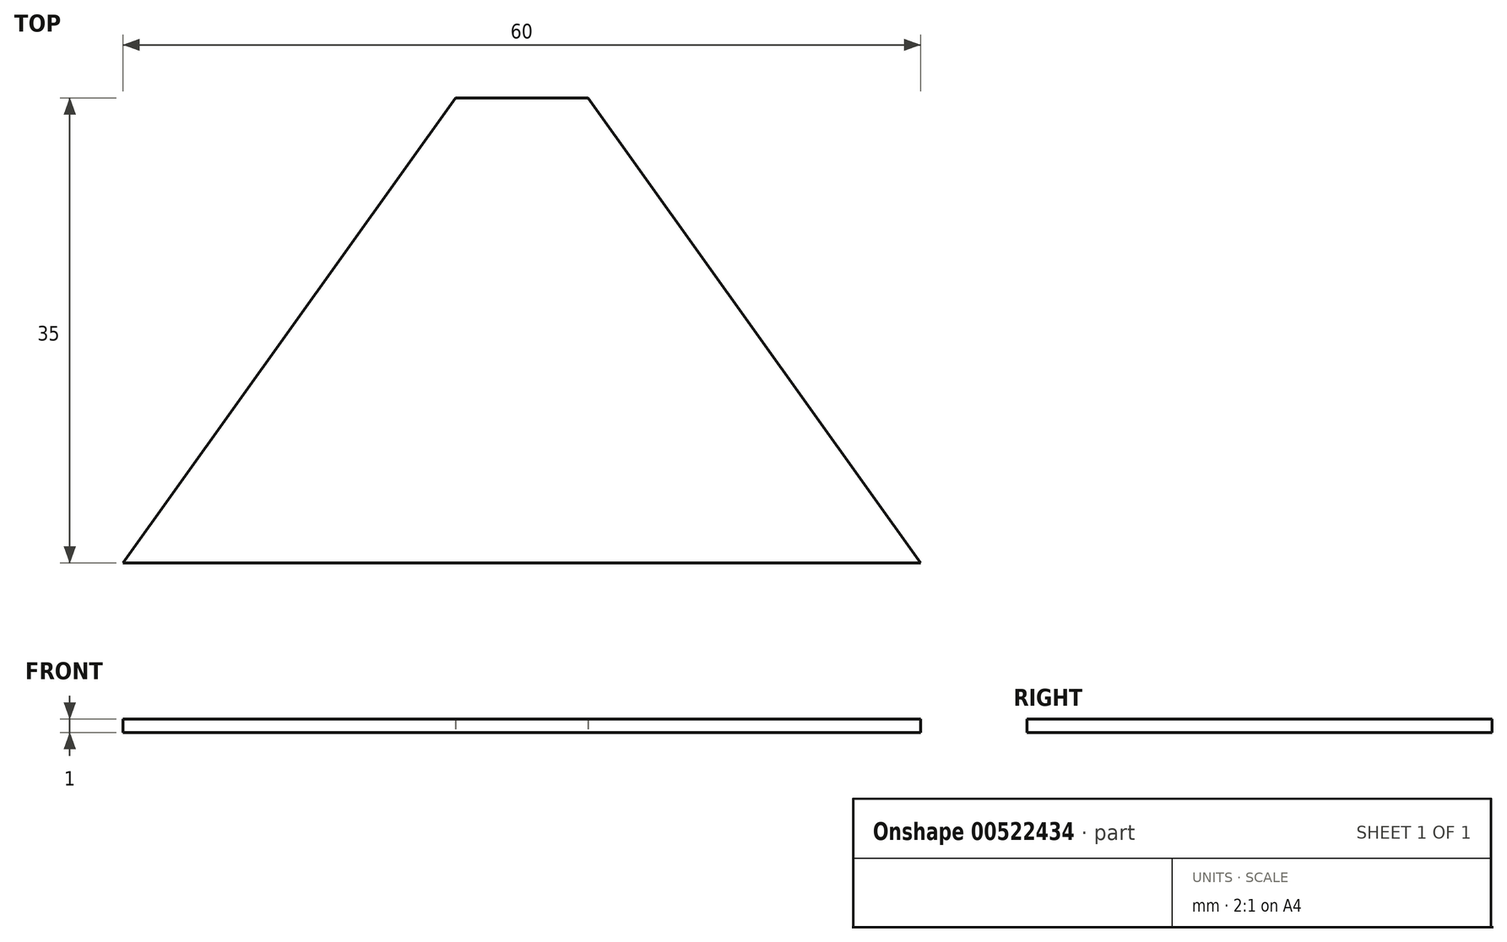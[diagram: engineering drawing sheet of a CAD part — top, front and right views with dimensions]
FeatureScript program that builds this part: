
annotation { "Feature Type Name" : "Feature", "Feature Type Description" : "" }
export const myFeature = defineFeature(function(context is Context, id is Id, definition is map)
    precondition{}
    {
        {
            var Q0;
            Q0=qCreatedBy(makeId("Top.planeOp"),FACE);
            var sketch = newSketch(context, id + "F0", { "sketchPlane" : qUnion([Q0])});
            skLineSegment(sketch, "E0.0", {"start": v(30, 0) * mm, "end": v(-30, 0) * mm});
            skLineSegment(sketch, "E0.1", {"start": v(-30, 0) * mm, "end": v(-5, 35) * mm});
            skLineSegment(sketch, "E0.2", {"start": v(5, 35) * mm, "end": v(30, 0) * mm});
            skPoint(sketch, "E0.0.midPoint", {"position": v(0, 0) * mm});
            skLineSegment(sketch, "E1", {"start": v(-5, 35) * mm, "end": v(5, 35) * mm});
            skPoint(sketch, "E2.orphan", {"position": v(0, 42) * mm});
            skLineSegment(sketch, "E3.0", {"start": v(160.36, 0) * mm, "end": v(70.36, 0) * mm});
            skLineSegment(sketch, "E3.1", {"start": v(70.36, 0) * mm, "end": v(107.86, 52.5) * mm});
            skLineSegment(sketch, "E3.2", {"start": v(122.86, 52.5) * mm, "end": v(160.36, 0) * mm});
            skPoint(sketch, "E3.0.midPoint", {"position": v(115.36, 0) * mm});
            skLineSegment(sketch, "E4", {"start": v(107.86, 52.5) * mm, "end": v(122.86, 52.5) * mm});
            skPoint(sketch, "E5.orphan", {"position": v(115.36, 63) * mm});
            skLineSegment(sketch, "E6.0", {"start": v(295.51, 0) * mm, "end": v(175.51, 0) * mm});
            skLineSegment(sketch, "E6.1", {"start": v(175.51, 0) * mm, "end": v(225.51, 70) * mm});
            skLineSegment(sketch, "E6.2", {"start": v(245.51, 70) * mm, "end": v(295.51, 0) * mm});
            skPoint(sketch, "E6.0.midPoint", {"position": v(235.51, 0) * mm});
            skLineSegment(sketch, "E7", {"start": v(225.51, 70) * mm, "end": v(245.51, 70) * mm});
            skPoint(sketch, "E8.orphan", {"position": v(235.51, 84) * mm});
            skSolve(sketch);
        }
        {
            var Q0;
            Q0=makeQuery(id+"F0.imprint","IMPRINT",FACE,{"disambiguationData":[TD([[makeQuery(id+"F0.imprint","IMPRINT",EDGE,{"derivedFrom":sQuery(id+"F0.wireOp",EDGE,"E0.0")}),-1.0]])]});
            extrude(context, id + "F1", {"entities" : qUnion([Q0]), "depth" : 1 * mm, "offsetDistance" : 25 * mm});
        }
    });
